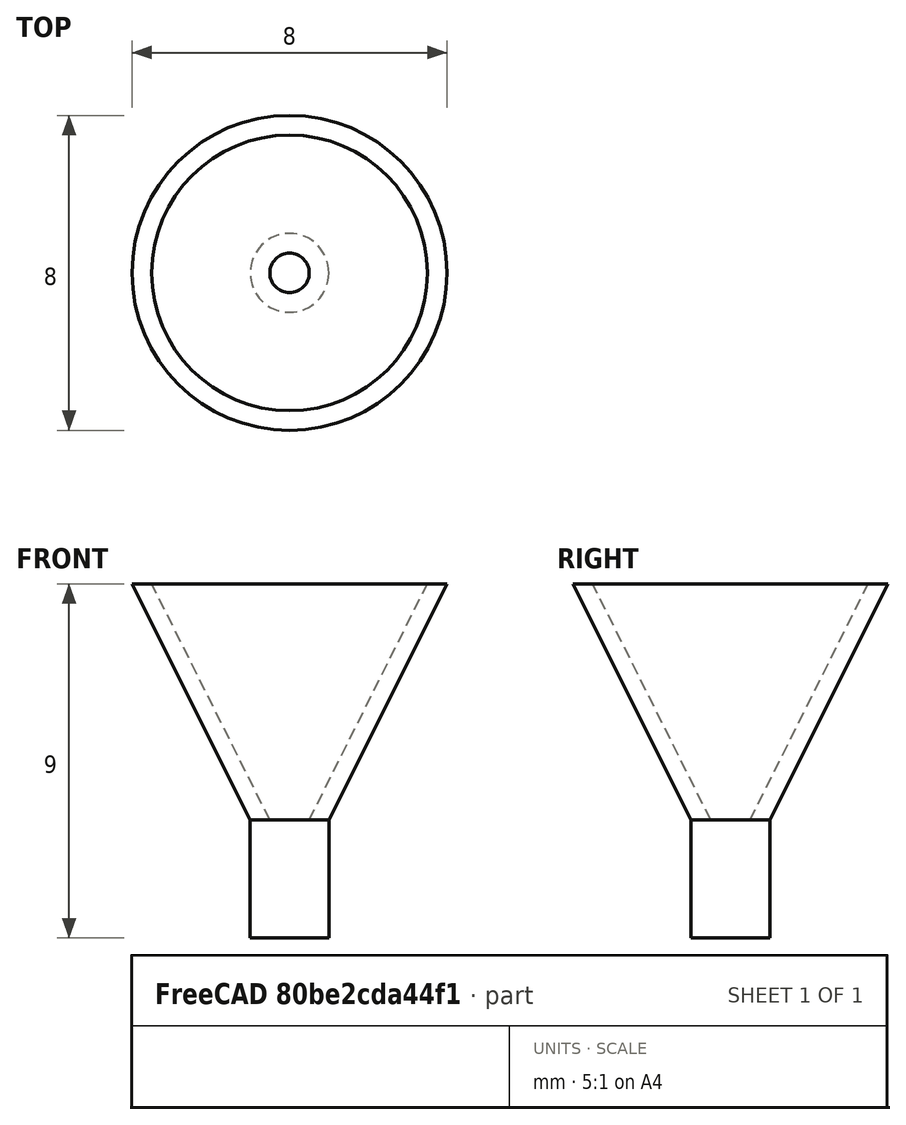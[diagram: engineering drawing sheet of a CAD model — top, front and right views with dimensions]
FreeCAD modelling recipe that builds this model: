
FCSTD DOCUMENT  (FreeCAD 0.21R33694 (Git))
Label: OJT1_T14R03_emut
License: All rights reserved
LicenseURL: http://en.wikipedia.org/wiki/All_rights_reserved
objects: Part::Cylinder×2, Part::Cut×2, Part::Cone×2, Part::MultiFuse×1
note: 7 computed .brp shape members not serialized (recipe doc carries the construction recipe); baked Part::Feature solids carry a one-line shape summary decoded from their .brp

FEATURE [Part::Cylinder] Cylinder
  Angle = 360
  AttacherType = Attacher::AttachEngine3D
  FirstAngle = 0
  Height = 3
  Radius = 1
  SecondAngle = 0
FEATURE [Part::Cylinder] Cylinder001
  Angle = 360
  AttacherType = Attacher::AttachEngine3D
  FirstAngle = 0
  Height = 3
  Radius = 0.5
  SecondAngle = 0
FEATURE [Part::Cut] Cut
  Base = -> Cylinder
  Refine = true
  Tool = -> Cylinder001
FEATURE [Part::Cone] Cone
  Angle = 360
  AttacherType = Attacher::AttachEngine3D
  Height = 6
  Placement = pos=(0,0,3) rot=(0,0,1;0rad)
  Radius1 = 1
  Radius2 = 4
FEATURE [Part::Cone] Cone001
  Angle = 360
  AttacherType = Attacher::AttachEngine3D
  Height = 6
  Placement = pos=(0,0,3) rot=(0,0,1;0rad)
  Radius1 = 0.5
  Radius2 = 3.5
FEATURE [Part::Cut] Cut001
  Base = -> Cone
  Refine = true
  Tool = -> Cone001
FEATURE [Part::MultiFuse] Fusion
  Refine = true
  Shapes = -> [Cut,Cut001,Cylinder,Cylinder001]
